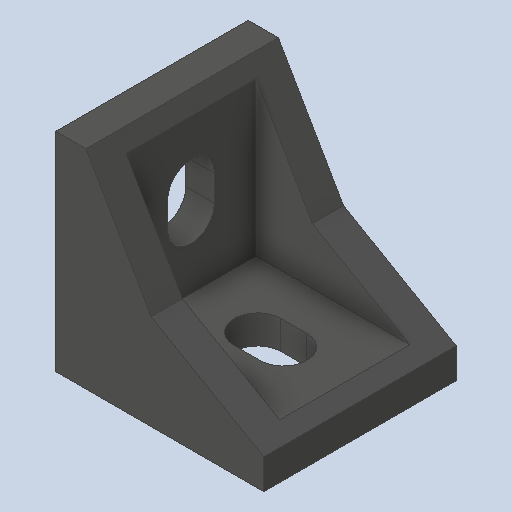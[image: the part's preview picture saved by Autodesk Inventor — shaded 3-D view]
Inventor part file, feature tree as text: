
AUTODESK INVENTOR PART (.ipt)
format: ipt  version: 2023 (Build 270158000, 158)  size: 165,376 bytes
history: native  units: mm
features: other x35, extrude x6, sketch x6
ambient origin geometry x8: Origin, YZ Plane, XZ Plane, XY Plane, X Axis, Y Axis, Z Axis, Center Point
bodies: Solid1 (feature_tree)
feature tree (47):
  extrude  "Extrusion1"  Depth=25.0mm TaperAngle=0.0deg
  extrude  "Extrusion2"  Depth=7.5mm TaperAngle=0.0deg
  extrude  "Extrusion3"  Depth=2.0mm TaperAngle=0.0deg
  extrude  "Extrusion4"  [1 undecoded]
  extrude  "Extrusion5"  [1 undecoded]
  extrude  "Extrusion6"  [1 undecoded]
  other  "GUS_4500_1_XY"
  other  "GUS_4500_1_YZ"
  other  "GUS_4500_1_ZX"
  other  "GUS_4500_1_X"
  other  "GUS_4500_1_Y"
  other  "GUS_4500_1_Z"
  other  "GUS_4500_1_Center"
  other  "GUS_4500_12_XY"
  other  "GUS_4500_12_YZ"
  other  "GUS_4500_12_ZX"
  other  "GUS_4500_12_X"
  other  "GUS_4500_12_Y"
  other  "GUS_4500_12_Z"
  other  "GUS_4500_12_Center"
  other  "GUS_4500_2_XY"
  other  "GUS_4500_2_YZ"
  other  "GUS_4500_2_ZX"
  other  "GUS_4500_2_X"
  other  "GUS_4500_2_Y"
  other  "GUS_4500_2_Z"
  other  "GUS_4500_2_Center"
  other  "GUS_4500_23_XY"
  other  "GUS_4500_23_YZ"
  other  "GUS_4500_23_ZX"
  other  "GUS_4500_23_X"
  other  "GUS_4500_23_Y"
  other  "GUS_4500_23_Z"
  other  "GUS_4500_23_Center"
  other  "p1_XY"
  other  "p1_YZ"
  other  "p1_ZX"
  other  "p1_X"
  other  "p1_Y"
  other  "p1_Z"
  other  "p1_Center"
  sketch  "Skizze_1"  dims[d0=37.0mm d1=0.0mm d2=25.0mm d3=0.0mm]
  sketch  "Skizze_2"  dims[d4=7.5mm d5=0.0mm d6=7.5mm d7=0.0mm]
  sketch  "Skizze_3"  dims[d8=2.0mm d9=0.0mm d10=2.0mm d11=0.0mm]
  sketch  "Skizze_4"  dims[d12=0.0mm d13=0.0mm d14=0.0mm d15=0.0mm d16=0.0mm]
  sketch  "Skizze_5"
  sketch  "Skizze_6"
note: 3 required parameter values undecoded (feature->parameter linkage not recoverable at this tier; creation-order binding heuristic only, values carry confidence <= 0.55)
